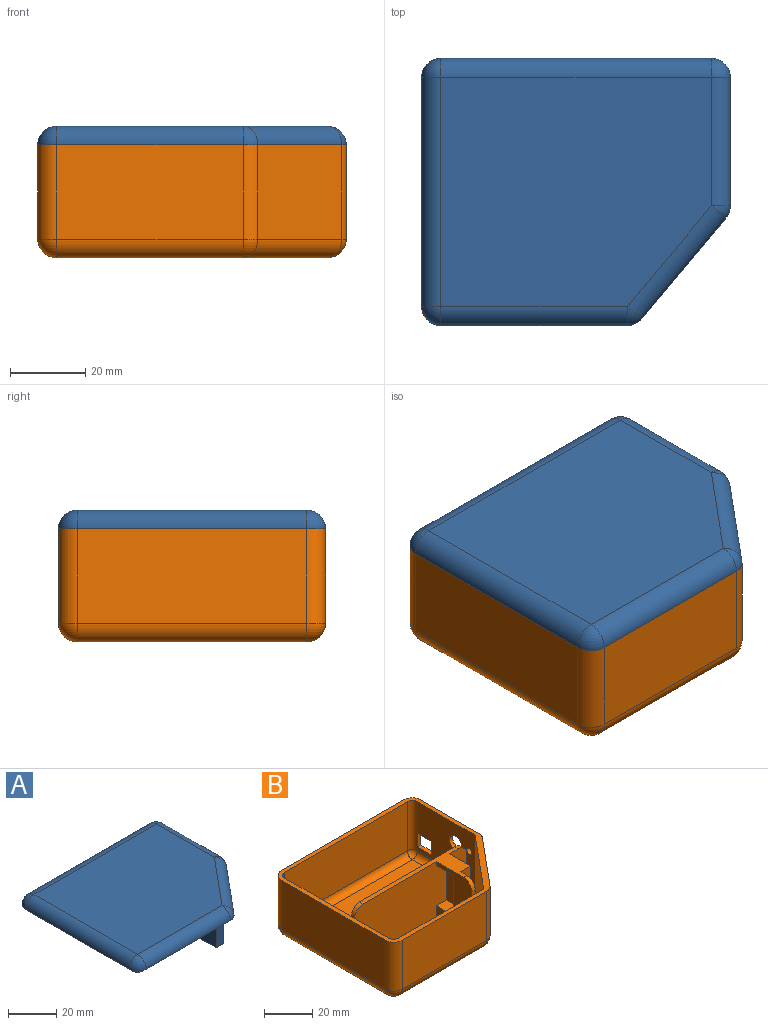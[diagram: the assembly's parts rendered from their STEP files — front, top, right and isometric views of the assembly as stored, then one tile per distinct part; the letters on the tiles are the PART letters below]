
ASSEMBLY  parts=2 mates=1
PART A: 41 faces, bbox 82x71x32 mm
  f0: plane 27x12.5mm, normal (1,0,0), area 161.7mm2, adj f1,f2,f3,f32,f34,f35,f36,f37
  f1: plane 14.09x11.74mm, normal (-0.77,0.64,0), area 36.7mm2, adj f0,f2,f3,f21
  f2: plane 78x67mm, normal (0,0,-1), area 134mm2, adj f0,f1,f16,f17,f18,f19,f20,f21
  f3: plane 77x66mm, normal (0,0,-1), area 4657.9mm2, adj f0,f1,f16,f17,f18,f19,f20,f21
  f4: plane 82x71mm, normal (0,0,-1), area 584.6mm2, adj f6,f7,f8,f9,f10,f11,f12,f13
  f5: plane 72x61mm, normal (0,0,1), area 4092.5mm2, adj f6,f9,f10,f13,f14
  f6: cylinder r=5mm len=49.66mm, axis (-1,0,0), area 390mm2, adj f4,f5,f7,f8
  f7: sphere r=5mm, area 21.9mm2, adj f4,f6,f9
  f8: sphere r=5mm, area 39.3mm2, adj f4,f6,f10
  f9: cylinder r=5mm len=30.01mm, axis (-0.64,-0.77,0), area 274.1mm2, adj f4,f5,f7,f11
  f10: cylinder r=5mm len=61mm, axis (0,1,0), area 479.1mm2, adj f4,f5,f8,f12
  f11: sphere r=5mm, area 17.4mm2, adj f4,f9,f13
  f12: sphere r=5mm, area 39.3mm2, adj f4,f10,f14
  f13: cylinder r=5mm len=34.19mm, axis (0,-1,0), area 268.5mm2, adj f4,f5,f11,f15
  f14: cylinder r=5mm len=72mm, axis (1,0,0), area 565.5mm2, adj f4,f5,f12,f15
  f15: sphere r=5mm, area 39.3mm2, adj f4,f13,f14
  f16: cylinder r=2.5mm len=2.5mm, axis (0,0,1), area 7.9mm2, adj f2,f3,f17,f31
  f17: plane 61x2mm, normal (1,0,0), area 122mm2, adj f2,f3,f16,f18
  f18: cylinder r=2.5mm len=2.5mm, axis (0,0,1), area 7.9mm2, adj f2,f3,f17,f19
  f19: plane 72x2mm, normal (0,-1,0), area 144mm2, adj f2,f3,f18,f20
  f20: cylinder r=2.5mm len=2.5mm, axis (0,0,1), area 7.9mm2, adj f2,f3,f19,f21
  f21: plane 33.82x2mm, normal (-1,0,0), area 67.6mm2, adj f1,f2,f3,f20
  f22: plane 14.81x12.34mm, normal (-0.77,0.64,0), area 38.6mm2, adj f2,f3,f31,f32
  f23: plane 50x2mm, normal (0,-1,0), area 100mm2, adj f2,f4,f24,f30
  f24: plane 30x25mm, normal (0.77,-0.64,0), area 78.1mm2, adj f2,f4,f23,f25
  f25: plane 34x2mm, normal (1,0,0), area 68mm2, adj f2,f4,f24,f26
  f26: cylinder r=3mm len=3mm, axis (0,0,1), area 9.4mm2, adj f2,f4,f25,f27
  f27: plane 72x2mm, normal (0,1,0), area 144mm2, adj f2,f4,f26,f28
  f28: cylinder r=3mm len=3mm, axis (0,0,1), area 9.4mm2, adj f2,f4,f27,f29
  f29: plane 61x2mm, normal (-1,0,0), area 122mm2, adj f2,f4,f28,f30
  f30: cylinder r=3mm len=3mm, axis (0,0,1), area 9.4mm2, adj f2,f4,f23,f29
  f31: plane 49.77x2mm, normal (0,1,0), area 99.5mm2, adj f2,f3,f16,f22
  f32: plane 27x4.26mm, normal (0,-1,0), area 113.7mm2, adj f0,f2,f3,f22,f33,f35
  f33: plane 27x12.5mm, normal (-1,0,0), area 337.5mm2, adj f3,f32,f34,f35
  f34: plane 27x4.26mm, normal (0,1,0), area 115mm2, adj f0,f3,f33,f35
  f35: plane 12.5x4.26mm, normal (0,0,-1), area 53.2mm2, adj f0,f32,f33,f34
  f36: plane 20.5x3mm, normal (0,-1,0), area 61.5mm2, adj f0,f37,f39,f40
  f37: plane 8.5x3mm, normal (0,0,-1), area 25.5mm2, adj f0,f36,f38,f40
  f38: plane 20.5x3mm, normal (0,1,0), area 61.5mm2, adj f0,f37,f39,f40
  f39: plane 8.5x3mm, normal (0,0,1), area 25.5mm2, adj f0,f36,f38,f40
  f40: plane 20.5x8.5mm, normal (1,0,0), area 174.2mm2, adj f36,f37,f38,f39
PART B: 64 faces, bbox 82x71x30 mm
  f0: plane 8x2mm, normal (0,0,1), area 16mm2, adj f8,f13,f16,f63
  f1: plane 8x2mm, normal (0,0,-1), area 16mm2, adj f8,f13,f16,f63
  f2: plane 28x10mm, normal (0,-1,0), area 274.6mm2, adj f4,f6,f52,f53,f57
  f3: plane 28x8.5mm, normal (1,0,0), area 232.6mm2, adj f4,f6,f49,f54,f56
  f4: plane 75x64mm, normal (0,0,1), area 3924mm2, adj f2,f3,f7,f11,f21,f22,f23,f42
  f5: plane 82x71mm, normal (0,0,1), area 584.6mm2, adj f8,f9,f12,f13,f14,f15,f18,f19
  f6: plane 56x18mm, normal (0,0,1), area 219mm2, adj f2,f3,f7,f11,f22,f53,f54,f55
  f7: plane 66x28mm, normal (0,1,0), area 1837.3mm2, adj f4,f6,f23,f52,f53,f55
  f8: plane 34.19x25mm, normal (1,0,0), area 747.5mm2, adj f0,f1,f5,f17,f26,f28,f32,f62
  f9: plane 61x25mm, normal (-1,0,0), area 1525mm2, adj f5,f24,f27,f40
  f10: plane 72x61mm, normal (0,0,-1), area 4092.5mm2, adj f32,f35,f36,f39,f40
  f11: plane 54x28mm, normal (0,-1,0), area 1461.6mm2, adj f4,f6,f22,f23,f55,f58,f59,f61
  f12: plane 72x25mm, normal (0,-1,0), area 1800mm2, adj f5,f30,f31,f46
  f13: plane 34x25mm, normal (-1,0,0), area 742.8mm2, adj f0,f1,f5,f17,f21,f31,f48,f62
  f14: plane 61x25mm, normal (1,0,0), area 1525mm2, adj f5,f29,f30,f44
  f15: plane 72x25mm, normal (0,1,0), area 1800mm2, adj f5,f26,f27,f36
  f16: plane 7x2mm, normal (0,-1,0), area 14mm2, adj f0,f1,f26,f31
  f17: cylinder r=3.75mm len=7.5mm, axis (-1,0,0), area 47.1mm2, adj f8,f13
  f18: plane 50x25mm, normal (0,1,0), area 1250mm2, adj f5,f21,f29,f42
  f19: plane 49.66x25mm, normal (0,-1,0), area 1241.5mm2, adj f5,f24,f25,f39
  f20: plane 26.81x25mm, normal (0.77,-0.64,0), area 872.5mm2, adj f5,f25,f28,f35
  f21: plane 30x28mm, normal (-0.77,0.64,0), area 1093.4mm2, adj f4,f5,f13,f18,f50,f51
  f22: plane 28x21mm, normal (-1,0,0), area 367.4mm2, adj f4,f6,f11,f49,f54,f58,f59,f60
  f23: plane 23x2mm, normal (-1,0,0), area 46mm2, adj f4,f7,f11,f55
  f24: cylinder r=5mm len=25mm, axis (0,0,1), area 196.3mm2, adj f5,f9,f19,f41
  f25: cylinder r=5mm len=25mm, axis (0,0,-1), area 109.5mm2, adj f5,f19,f20,f37
  f26: cylinder r=5mm len=25mm, axis (0,0,-1), area 196.3mm2, adj f5,f8,f15,f16,f34
  f27: cylinder r=5mm len=25mm, axis (0,0,1), area 196.3mm2, adj f5,f9,f15,f38
  f28: cylinder r=5mm len=25mm, axis (0,0,-1), area 86.8mm2, adj f5,f8,f20,f33
  f29: cylinder r=3mm len=25mm, axis (0,0,-1), area 117.8mm2, adj f5,f14,f18,f43
  f30: cylinder r=3mm len=25mm, axis (0,0,-1), area 117.8mm2, adj f5,f12,f14,f45
  f31: cylinder r=3mm len=25mm, axis (0,0,1), area 117.8mm2, adj f5,f12,f13,f16,f47
  f32: cylinder r=5mm len=34.19mm, axis (0,1,0), area 268.5mm2, adj f8,f10,f33,f34
  f33: sphere r=5mm, area 17.4mm2, adj f28,f32,f35
  f34: sphere r=5mm, area 39.3mm2, adj f26,f32,f36
  f35: cylinder r=5mm len=30.01mm, axis (0.64,0.77,0), area 274.1mm2, adj f10,f20,f33,f37
  f36: cylinder r=5mm len=72mm, axis (-1,0,0), area 565.5mm2, adj f10,f15,f34,f38
  f37: sphere r=5mm, area 21.9mm2, adj f25,f35,f39
  f38: sphere r=5mm, area 39.3mm2, adj f27,f36,f40
  f39: cylinder r=5mm len=49.66mm, axis (1,0,0), area 390mm2, adj f10,f19,f37,f41
  f40: cylinder r=5mm len=61mm, axis (0,-1,0), area 479.1mm2, adj f9,f10,f38,f41
  f41: sphere r=5mm, area 39.3mm2, adj f24,f39,f40
  f42: cylinder r=3mm len=50mm, axis (-1,0,0), area 235.6mm2, adj f4,f18,f43,f50
  f43: sphere r=3mm, area 14.1mm2, adj f29,f42,f44
  f44: cylinder r=3mm len=61mm, axis (0,1,0), area 287.5mm2, adj f4,f14,f43,f45
  f45: sphere r=3mm, area 14.1mm2, adj f30,f44,f46
  f46: cylinder r=3mm len=72mm, axis (-1,0,0), area 339.3mm2, adj f4,f12,f45,f47
  f47: sphere r=3mm, area 14.1mm2, adj f31,f46,f48
  f48: cylinder r=3mm len=34mm, axis (0,-1,0), area 160.2mm2, adj f4,f13,f47,f51
  f49: plane 23x2mm, normal (0,-1,0), area 46mm2, adj f3,f4,f22,f54
  f50: plane 3x3mm, normal (1,0,0), area 1.9mm2, adj f4,f21,f42
  f51: plane 3x3mm, normal (0,-1,0), area 1.9mm2, adj f4,f21,f48
  f52: plane 23x2mm, normal (1,0,0), area 46mm2, adj f2,f4,f7,f53
  f53: cylinder r=5mm len=5mm, axis (0,1,0), area 15.7mm2, adj f2,f6,f7,f52
  f54: cylinder r=5mm len=5mm, axis (1,0,0), area 15.7mm2, adj f3,f6,f22,f49
  f55: cylinder r=5mm len=5mm, axis (0,-1,0), area 15.7mm2, adj f6,f7,f11,f23
  f56: plane 28x6mm, normal (0,-1,0), area 168mm2, adj f3,f4,f6,f57
  f57: plane 28x12.5mm, normal (1,0,0), area 350mm2, adj f2,f4,f6,f56
  f58: plane 10.5x6mm, normal (0,0,-1), area 63mm2, adj f11,f22,f60,f61
  f59: plane 10.5x6mm, normal (0,0,1), area 63mm2, adj f11,f22,f60,f61
  f60: plane 20.5x6mm, normal (0,1,0), area 123mm2, adj f22,f58,f59,f61
  f61: plane 20.5x10.5mm, normal (-1,0,0), area 215.2mm2, adj f11,f58,f59,f60
  f62: cylinder r=1.5mm len=3mm, axis (1,0,0), area 18.8mm2, adj f8,f13
  f63: plane 7x2mm, normal (0,1,0), area 14mm2, adj f0,f1,f8,f13
PLACE A t=(-8.92,19.02,-50.55)mm
PLACE B t=(-8.92,19.02,-19.35)mm
MATE fastened A.f4 <-> B.f5  axis (0,0,-1) through (30.92,-2.88,10.65)mm
